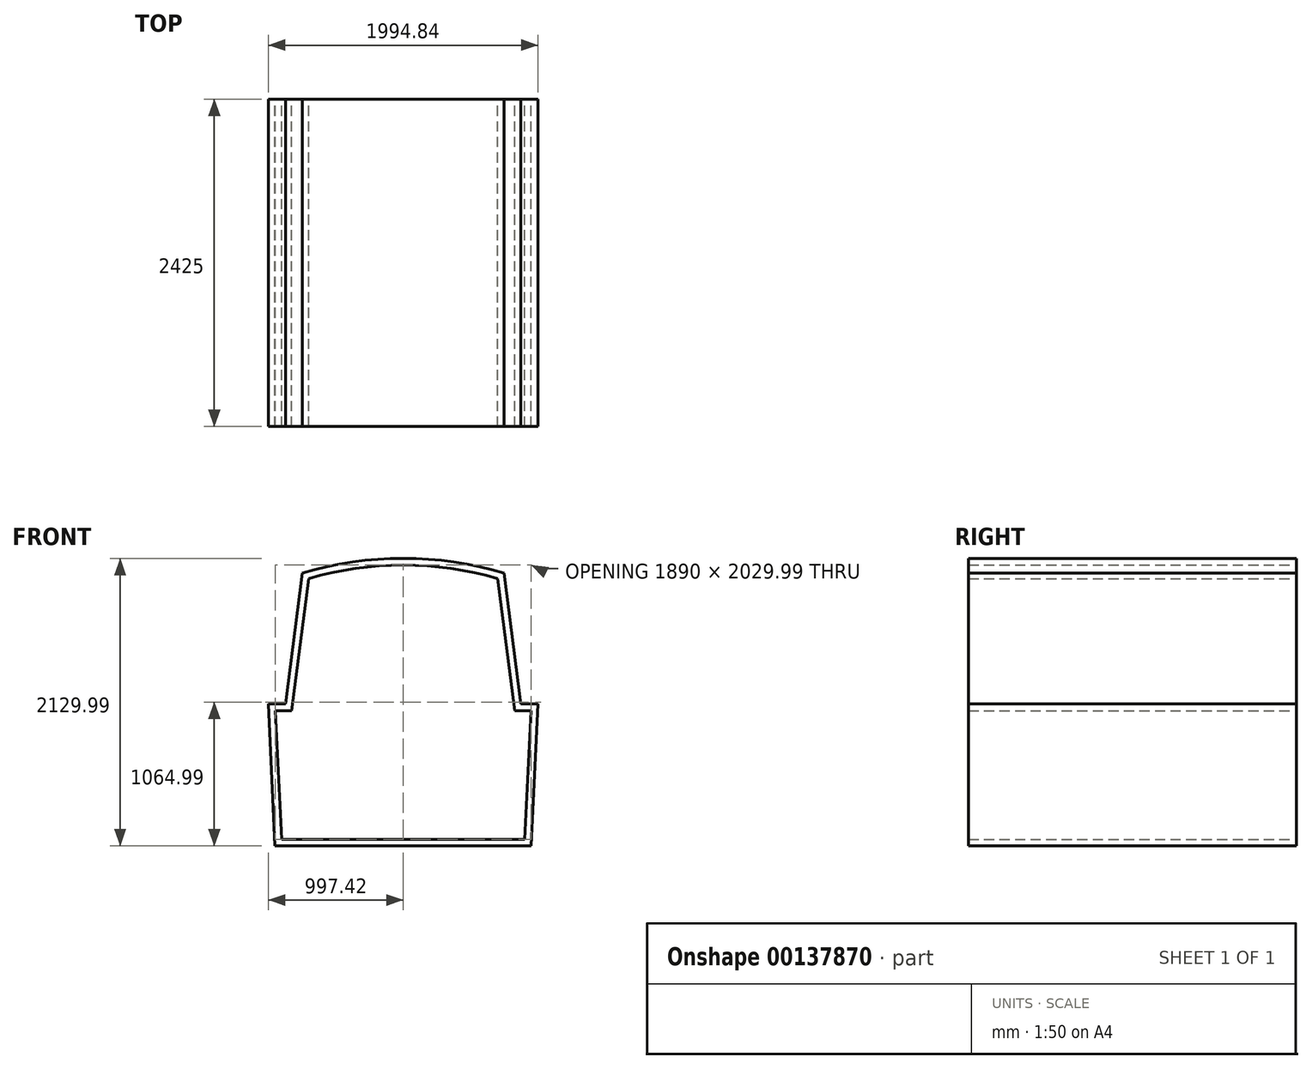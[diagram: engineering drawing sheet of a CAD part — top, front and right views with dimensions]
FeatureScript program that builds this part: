
annotation { "Feature Type Name" : "Feature", "Feature Type Description" : "" }
export const myFeature = defineFeature(function(context is Context, id is Id, definition is map)
    precondition{}
    {
        {
            var Q0;
            Q0=qCreatedBy(makeId("Front.planeOp"),FACE);
            var sketch = newSketch(context, id + "F0", { "sketchPlane" : qUnion([Q0])});
            skLineSegment(sketch, "E0", {"start": v(0, 0) * mm, "end": v(-900, 0) * mm});
            skLineSegment(sketch, "E1", {"start": v(-900, 0) * mm, "end": v(-945, 950.94) * mm});
            skLineSegment(sketch, "E2", {"start": v(-945, 950.94) * mm, "end": v(-825, 950.94) * mm});
            skLineSegment(sketch, "E3", {"start": v(-825, 950.94) * mm, "end": v(-700, 1929.99) * mm});
            skArc(sketch, "E4", {"start": v(0, 2029.99) * mm, "mid": v(-353.55, 2004.86) * mm, "end": v(-700, 1929.99) * mm});
            skLineSegment(sketch, "E5", {"start": v(0, 2029.99) * mm, "end": v(12.08, 2029.99) * mm, "construction": true});
            skLineSegment(sketch, "E6", {"start": v(-700, 1929.99) * mm, "end": v(382.66, 1929.99) * mm, "construction": true});
            skLineSegment(sketch, "E7", {"start": v(0, -50) * mm, "end": v(-947.69, -50) * mm});
            skLineSegment(sketch, "E8", {"start": v(-947.69, -50) * mm, "end": v(-997.42, 1000.94) * mm});
            skLineSegment(sketch, "E9", {"start": v(-997.42, 1000.94) * mm, "end": v(-869.02, 1000.94) * mm});
            skLineSegment(sketch, "E10", {"start": v(-869.02, 1000.94) * mm, "end": v(-745.4, 1969.22) * mm});
            skArc(sketch, "E11", {"start": v(0, 2079.99) * mm, "mid": v(-376.8, 2052.15) * mm, "end": v(-745.4, 1969.22) * mm});
            skLineSegment(sketch, "E12", {"start": v(0, 2079.99) * mm, "end": v(239.8, 2079.99) * mm, "construction": true});
            skLineSegment(sketch, "E13.MirrorCS", {"start": v(0, 2029.99) * mm, "end": v(-12.08, 2029.99) * mm, "construction": true});
            skLineSegment(sketch, "E14.MirrorCS", {"start": v(945, 950.94) * mm, "end": v(825, 950.94) * mm});
            skLineSegment(sketch, "E15.MirrorCS", {"start": v(997.42, 1000.94) * mm, "end": v(869.02, 1000.94) * mm});
            skLineSegment(sketch, "E16.MirrorCS", {"start": v(700, 1929.99) * mm, "end": v(-382.66, 1929.99) * mm, "construction": true});
            skLineSegment(sketch, "E17.MirrorCS", {"start": v(0, 2079.99) * mm, "end": v(-239.8, 2079.99) * mm, "construction": true});
            skLineSegment(sketch, "E18.MirrorCS", {"start": v(0, -50) * mm, "end": v(947.69, -50) * mm});
            skLineSegment(sketch, "E19.MirrorCS", {"start": v(900, 0) * mm, "end": v(945, 950.94) * mm});
            skArc(sketch, "E20.MirrorCS", {"start": v(0, 2079.99) * mm, "mid": v(376.8, 2052.15) * mm, "end": v(745.4, 1969.22) * mm});
            skLineSegment(sketch, "E21.MirrorCS", {"start": v(869.02, 1000.94) * mm, "end": v(745.4, 1969.22) * mm});
            skLineSegment(sketch, "E22.MirrorCS", {"start": v(825, 950.94) * mm, "end": v(700, 1929.99) * mm});
            skArc(sketch, "E23.MirrorCS", {"start": v(0, 2029.99) * mm, "mid": v(353.55, 2004.86) * mm, "end": v(700, 1929.99) * mm});
            skLineSegment(sketch, "E24.MirrorCS", {"start": v(0, 0) * mm, "end": v(900, 0) * mm});
            skLineSegment(sketch, "E25.MirrorCS", {"start": v(947.69, -50) * mm, "end": v(997.42, 1000.94) * mm});
            skSolve(sketch);
        }
        {
            var Q0;
            Q0=makeQuery(id+"F0.imprint","IMPRINT",FACE,{"disambiguationData":[TD([[makeQuery(id+"F0.imprint","IMPRINT",EDGE,{"derivedFrom":sQuery(id+"F0.wireOp",EDGE,"E0")}),1.0]])]});
            extrude(context, id + "F1", {"entities" : qUnion([Q0]), "depth" : 2425 * mm});
        }
    });
